# Revit family: OXeN X2-W-1.2-H podstropní_RFA2019
name_source: partatom
category: Mechanical Equipment
units: mm (PartAtom-declared; Revit-internal decimal feet)

## family parameters
Cut with Voids When Loaded = No
Host = Face
Part Type = Normal
Room Calculation Point = No
Round Connector Dimension = Use Diameter
Shared = No

## types (1)
- X2-W-1.2-H
    Air flow = 1200 m³/h
    Apparent power = 437 VA
    Assembly Code = 30032; podstropní; s teplovodním dohřevem - P=10kW při 80/60/5; (Qmax=1200m3/h při 100% vzduchovém výkonu a dpext=0Pa);
    Connection = 1/2"
    Default Elevation = 0 mm  [stored 0 ft]
    Description = Bezkanálová větrací jednotka s rekuperací
    Heating capacity = 0 kW
    IP = 42
    Inlet air temperature (Tp1) = 0 °C
    Inlet water temperature (Tw1) = 0 °C
    Load classification = Motor
    Manufacturer = Hydronic Systems Prague s.r.o.
    Material = FLOWAIR-EPP-Gray
    Max. current consumption = 2 A
    Model = OXeN X2-W-1.2-H
    Outlet air temperature (Tp2) = 0 °C
    Outlet water temperature (Tw2) = 0 °C
    Power ratio = 0.98
    Power supply = 230 V
    Type Comments = podstropní instalace; výměník PN16; twmax=95°C; regulace vzduchového výkonu - spojitá 0-100%; filtr =EU4; IP42; vertikální neizotermický (dt=5K) dosah pro koncovou rychlost 0,2m/s =max.4,5m
    URL = www.hydronic.cz
    Water pressure drop in the heat exchanger = 0 kPa
    Water stream flow in the heat exchanger = 0 L/s
    Weight of unit = 72.60 kg
    Weight of unit filled with water = 73.40 kg

note: [stored X ft] marks values corroborated as IEEE doubles in the binary element streams (Revit-internal decimal feet)
